# Revit family: POR_Ulysse_T3190_BIM_FR
name_source: partatom
category: Plumbing Fixtures
revit_build: Autodesk Revit 2017 (Build: 20160225_1515(x64)
units: mm (PartAtom-declared; Revit-internal decimal feet)

## family parameters
Always vertical = No
Cut with Voids When Loaded = No
OmniClass Number = 23.45.05.14.21
OmniClass Title = Bathtubs
Part Type = Normal
Room Calculation Point = No
Round Connector Dimension = Use Diameter
Shared = No
Work Plane-Based = No

## types (1)
- T3190AA - ULYSSE - Lumière LED
    Accessoires = www.idealstandard.be
    Auteur = Ideal Standard
    BOSUseNativeGeometries = 1
    Bim-NomDuProjet = POR_Porcher_Storage_T3190AA
    Caractéristiques = Lumière LED - 1x5,5 W
    CodeBarre = 8014140447078
    ConseilsDInstallation = www.idealstandard.be
    Cost = 0 $
    Couleur = Chrome
    CoûtDeRemplacement = 0
    DateDeCréation = 2018_08_15
    Description = ULYSSE - Lumière LED
    Dimensions = 42 x 280 x 121mm
    DuréeGarantie = ans
    DétailGarantie = Constructeur
    Espace = Interne
    Forme = Complexe
    Hauteur = 42 mm
    IfcExportAs = IfcSanitaryTerminalType
    IfcExportType = Storage
    InformationsProduit = www.idealstandard.be
    Largeur = 280 mm  [stored 0.918635 ft]
    LienUtile = www.idealstandard.be
    Longueur = 121 mm
    Manufacturer = www.idealstandard.be
    Marque = PORCHER
    Matériel = Glass
    Model = T3190AA
    Nom = POR_Porcher_Storage_T3190AA
    PerformanceAccessibilité = NF
    PoidsNet = 0.19 Kg
    Profondeur = 0 mm  [stored 0 ft]
    Raccordement = Plomberie
    Référence = T3190AA
    Révision = 1
    TypeDImmobilisation = Fixe
    URL = www.idealstandard.be
    Uniclass2015Code = Pr_40_20_76_94
    Uniclass2015Title = Vanity units
    Uniclass2015Version = Products v1.1
    UnitéDeTemps = an
    UrlDuFabricant = www.idealstandard.be
    Version = 1

note: [stored X ft] marks values corroborated as IEEE doubles in the binary element streams (Revit-internal decimal feet)

## geometry (parser evidence)
native form markers: Sweep x1
no freeform markers — native parametric forms only
